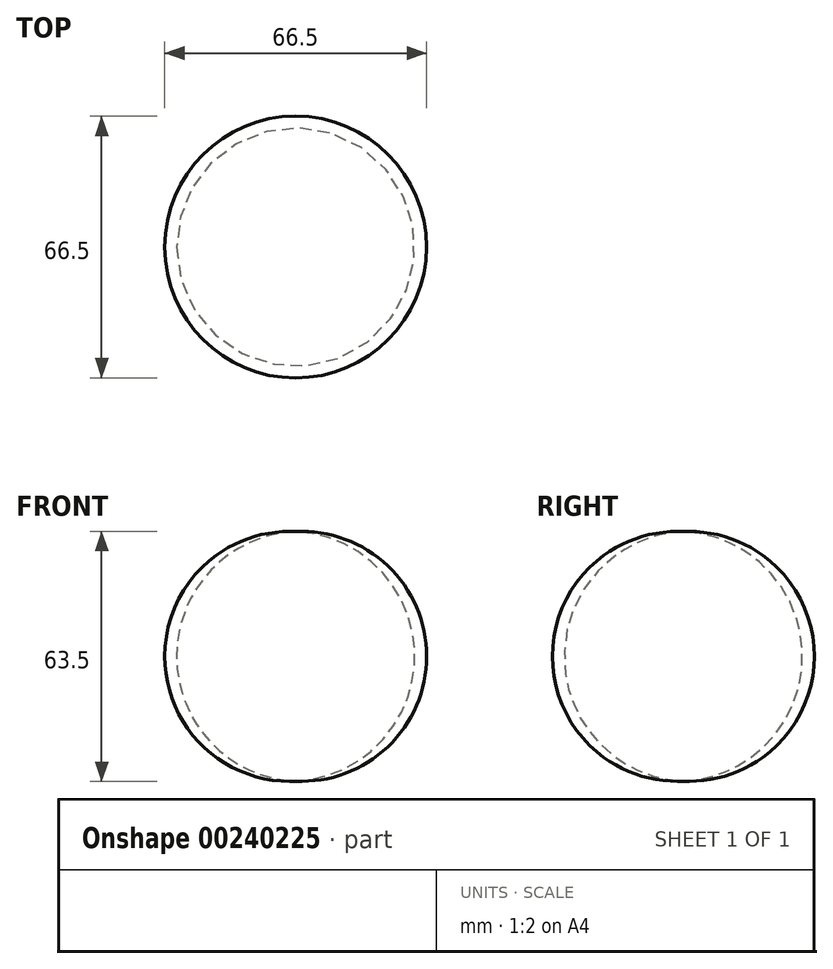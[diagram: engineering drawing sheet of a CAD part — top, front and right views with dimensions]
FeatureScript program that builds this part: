
annotation { "Feature Type Name" : "Feature", "Feature Type Description" : "" }
export const myFeature = defineFeature(function(context is Context, id is Id, definition is map)
    precondition{}
    {
        {
            var Q0;
            Q0=qCreatedBy(makeId("Front.planeOp"),FACE);
            var sketch = newSketch(context, id + "F0", { "sketchPlane" : qUnion([Q0])});
            skArc(sketch, "E0", {"start": v(0, 31.71) * mm, "mid": v(-30.25, 0) * mm, "end": v(0, -31.71) * mm});
            skLineSegment(sketch, "E1", {"start": v(0, 31.71) * mm, "end": v(0, -31.71) * mm});
            skSolve(sketch);
        }
        {
            var Q0;
            Q0 = qSketchRegion(id + "F0", true);
            var Q1;
            Q1=sQuery(id+"F0.wireOp",EDGE,"E1");
            revolve(context, id + "F1", {"entities" : qUnion([Q0]), "axis" : qUnion([Q1]), "revolveType" : RevolveType.FULL});
        }
    });
